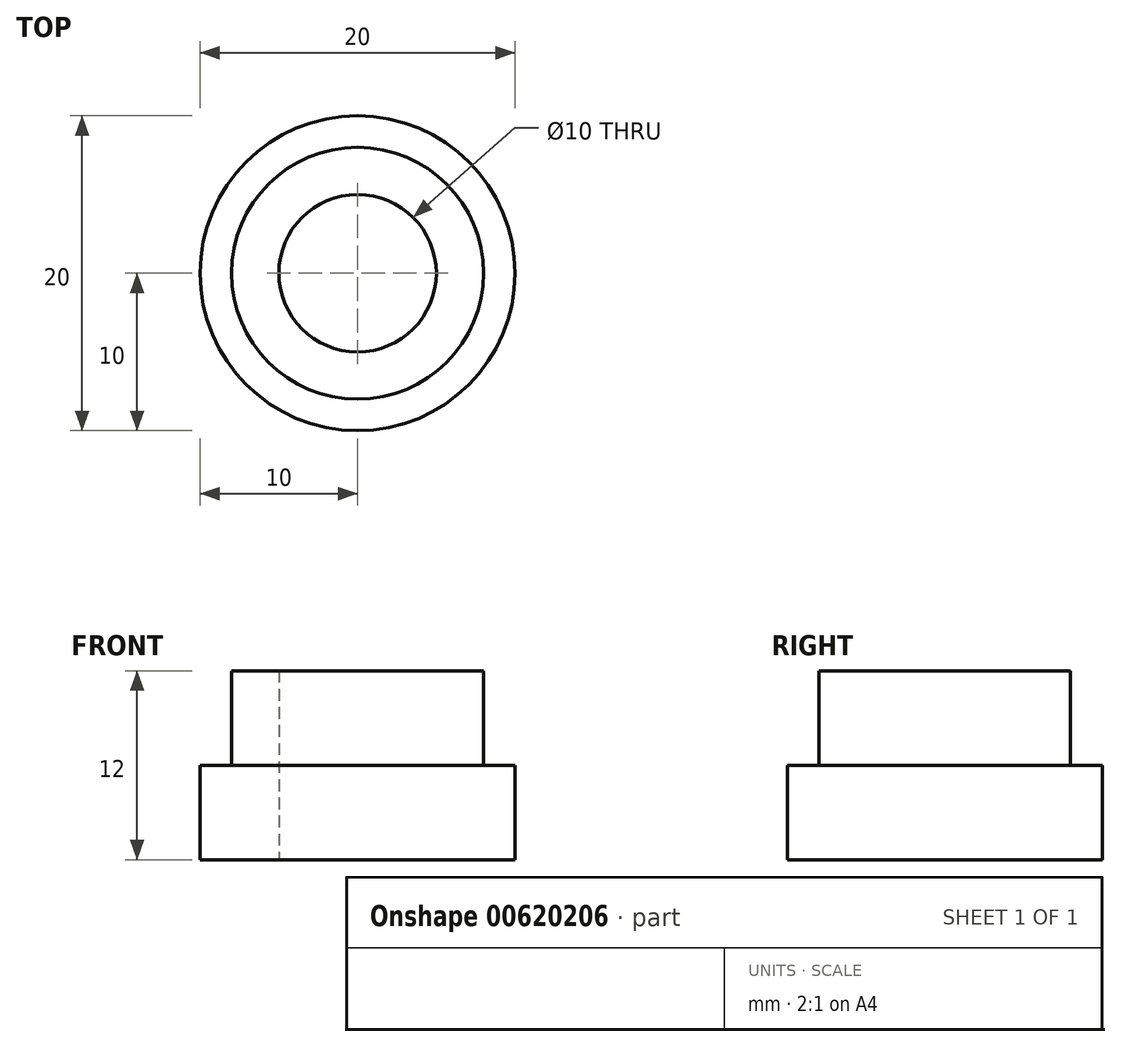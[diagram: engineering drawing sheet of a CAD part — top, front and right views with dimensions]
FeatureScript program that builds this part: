
annotation { "Feature Type Name" : "Feature", "Feature Type Description" : "" }
export const myFeature = defineFeature(function(context is Context, id is Id, definition is map)
    precondition{}
    {
        {
            var Q0;
            Q0=qCreatedBy(makeId("Right.planeOp"),FACE);
            var sketch = newSketch(context, id + "F0", { "sketchPlane" : qUnion([Q0])});
            skLineSegment(sketch, "E0", {"start": v(0, 0) * mm, "end": v(0, 21.96) * mm, "construction": true});
            skLineSegment(sketch, "E1", {"start": v(-10, 0) * mm, "end": v(-10, 6) * mm});
            skLineSegment(sketch, "E2", {"start": v(-10, 6) * mm, "end": v(-8, 6) * mm});
            skLineSegment(sketch, "E3", {"start": v(-8, 6) * mm, "end": v(-8, 12) * mm});
            skLineSegment(sketch, "E4", {"start": v(-8, 12) * mm, "end": v(-5, 12) * mm});
            skLineSegment(sketch, "E5", {"start": v(-5, 12) * mm, "end": v(-5, 0) * mm});
            skLineSegment(sketch, "E6", {"start": v(-5, 0) * mm, "end": v(-10, 0) * mm});
            skSolve(sketch);
        }
        {
            var Q0;
            Q0=makeQuery(id+"F0.imprint","IMPRINT",FACE,{"disambiguationData":[TD([[makeQuery(id+"F0.imprint","IMPRINT",EDGE,{"derivedFrom":sQuery(id+"F0.wireOp",EDGE,"E1")}),-1.0]])]});
            var Q1;
            Q1=sQuery(id+"F0.wireOp",EDGE,"E0");
            revolve(context, id + "F1", {"entities" : qUnion([Q0]), "axis" : qUnion([Q1]), "revolveType" : RevolveType.FULL});
        }
    });
